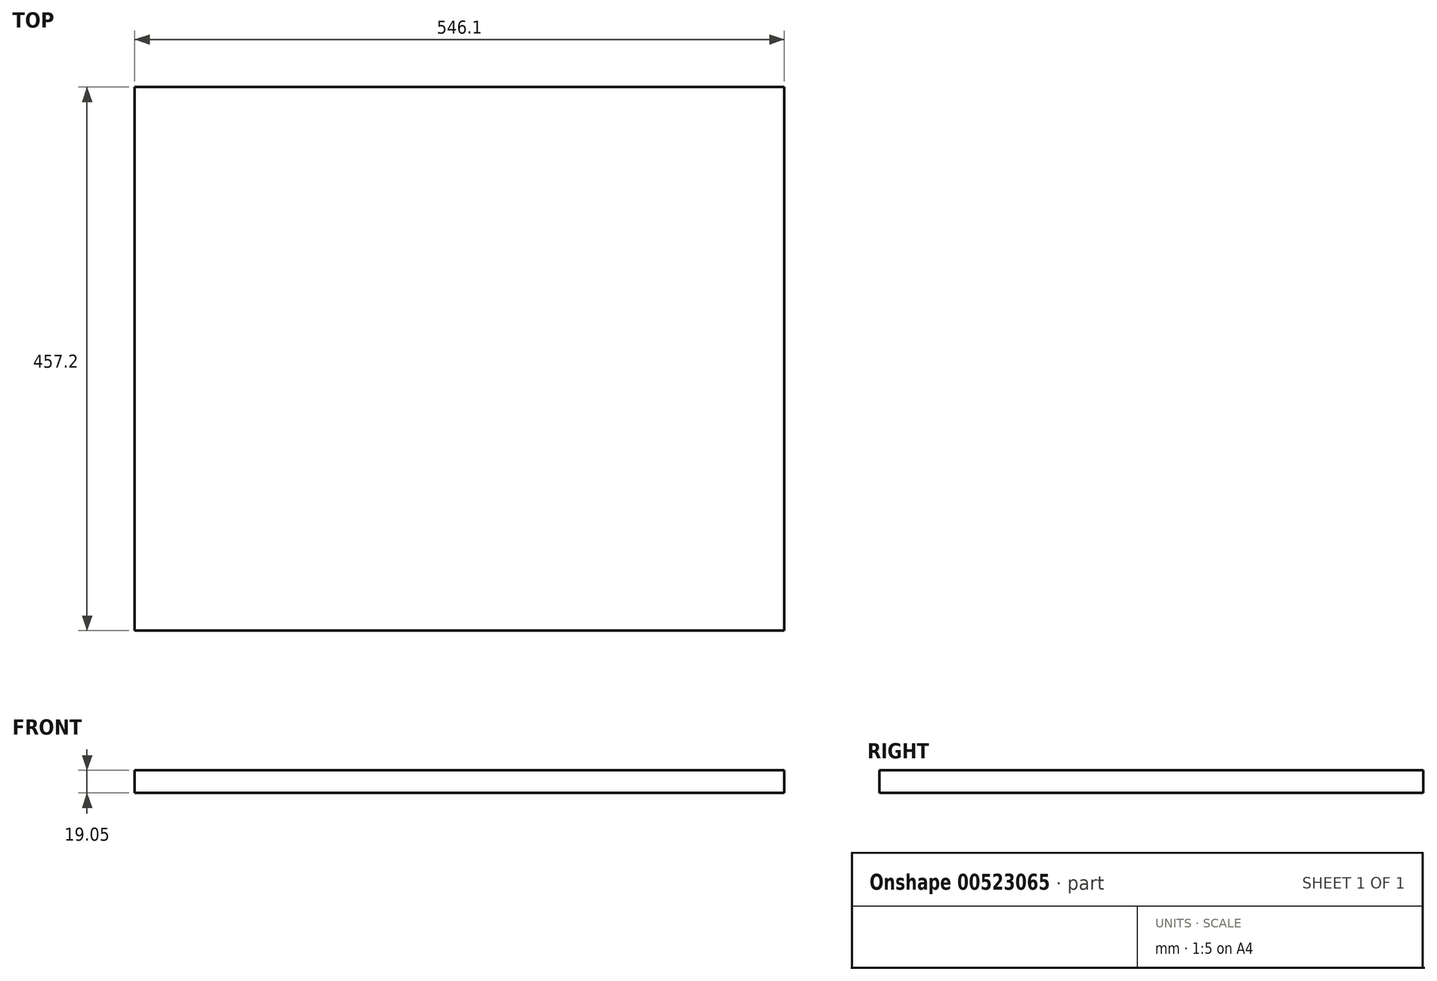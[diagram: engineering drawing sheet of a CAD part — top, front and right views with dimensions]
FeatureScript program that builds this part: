
annotation { "Feature Type Name" : "Feature", "Feature Type Description" : "" }
export const myFeature = defineFeature(function(context is Context, id is Id, definition is map)
    precondition{}
    {
        {
            var Q0;
            Q0=qCreatedBy(makeId("Top.planeOp"),FACE);
            var sketch = newSketch(context, id + "F0", { "sketchPlane" : qUnion([Q0])});
            skLineSegment(sketch, "E0.bottom", {"start": v(0, 0) * mm, "end": v(546.1, 0) * mm});
            skLineSegment(sketch, "E0.top", {"start": v(0, 457.2) * mm, "end": v(546.1, 457.2) * mm});
            skLineSegment(sketch, "E0.left", {"start": v(0, 0) * mm, "end": v(0, 457.2) * mm});
            skLineSegment(sketch, "E0.right", {"start": v(546.1, 0) * mm, "end": v(546.1, 457.2) * mm});
            skSolve(sketch);
        }
        {
            var Q0;
            Q0=qSketchRegion(id+"F0",true);
            extrude(context, id + "F1", {"entities" : qUnion([Q0]), "depth" : 19.05 * mm, "offsetDistance" : 25.4 * mm});
        }
    });
